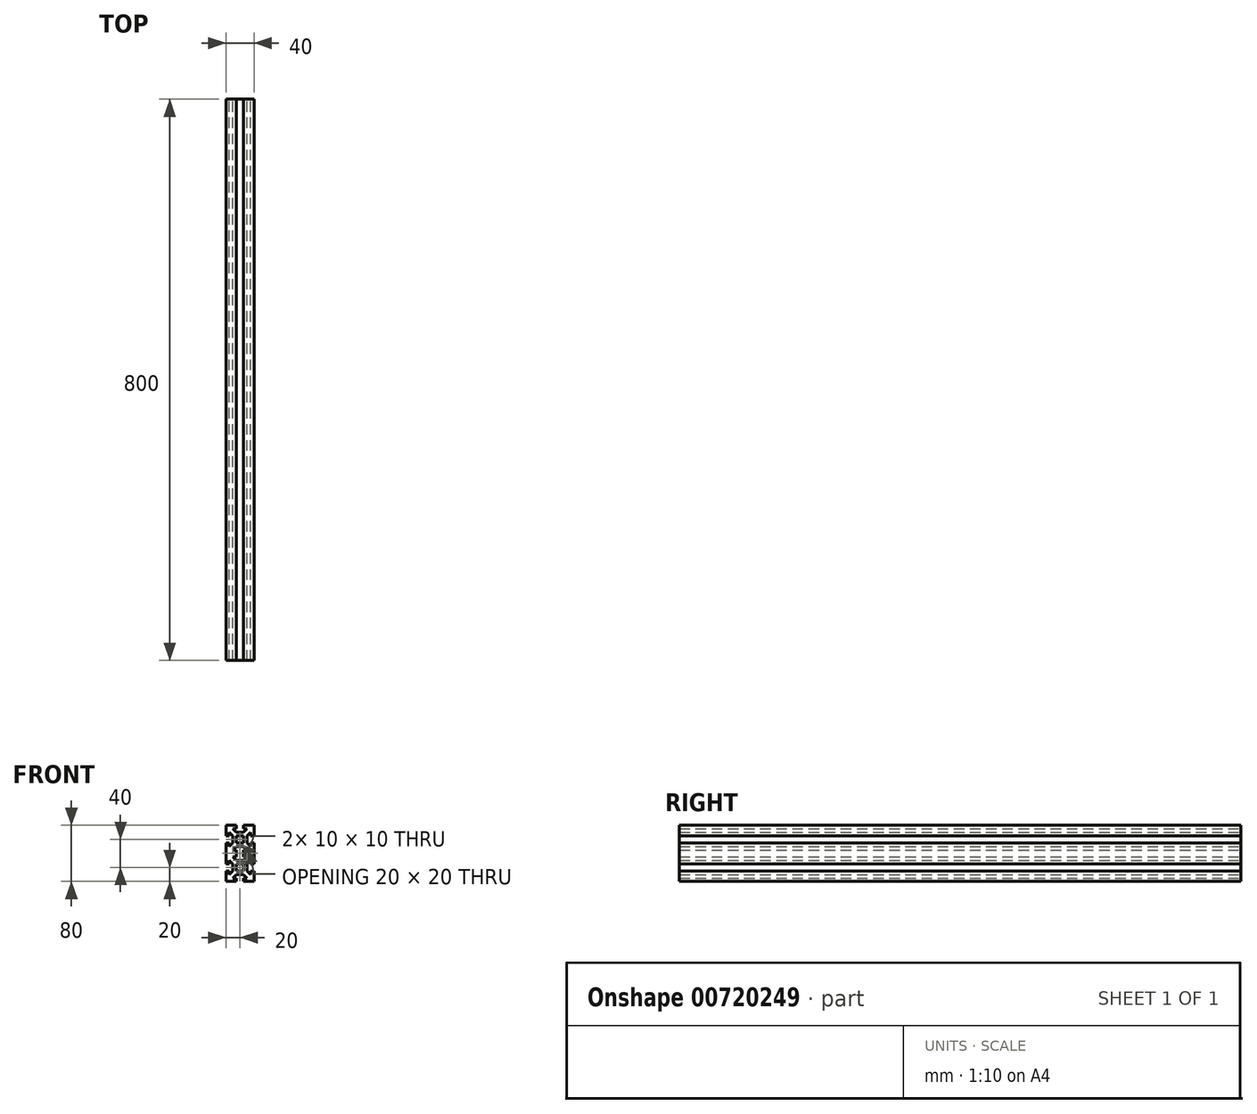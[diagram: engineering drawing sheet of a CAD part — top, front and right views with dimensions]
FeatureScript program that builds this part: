
annotation { "Feature Type Name" : "Feature", "Feature Type Description" : "" }
export const myFeature = defineFeature(function(context is Context, id is Id, definition is map)
    precondition{}
    {
        {
            var Q0;
            Q0=qCreatedBy(makeId("Front.planeOp"),FACE);
            var sketch = newSketch(context, id + "F0", { "sketchPlane" : qUnion([Q0])});
            skLineSegment(sketch, "E0.top", {"start": v(20, -20) * mm, "end": v(5, -20) * mm});
            skLineSegment(sketch, "E0.left", {"start": v(20, 20) * mm, "end": v(20, 5) * mm});
            skLineSegment(sketch, "E0.right", {"start": v(-20, 20) * mm, "end": v(-20, 5) * mm});
            skPoint(sketch, "E0.middle", {"position": v(0, 0) * mm});
            skLineSegment(sketch, "E1", {"start": v(0, 20) * mm, "end": v(0, -20) * mm, "construction": true});
            skLineSegment(sketch, "E2", {"start": v(-20, 0) * mm, "end": v(20, 0) * mm, "construction": true});
            skLineSegment(sketch, "E3", {"start": v(-20, 5) * mm, "end": v(-15, 5) * mm});
            skLineSegment(sketch, "E4", {"start": v(-20, -5) * mm, "end": v(-15, -5) * mm});
            skLineSegment(sketch, "E5", {"start": v(-5, 20) * mm, "end": v(-5, 15) * mm});
            skLineSegment(sketch, "E6", {"start": v(5, 20) * mm, "end": v(5, 15) * mm});
            skLineSegment(sketch, "E7", {"start": v(-10, 15) * mm, "end": v(-5, 15) * mm});
            skLineSegment(sketch, "E8", {"start": v(-10, -15) * mm, "end": v(-5, -15) * mm});
            skLineSegment(sketch, "E9", {"start": v(15, 10) * mm, "end": v(15, 5) * mm});
            skLineSegment(sketch, "E10", {"start": v(-15, 10) * mm, "end": v(-10, 5) * mm});
            skLineSegment(sketch, "E11", {"start": v(-10, 15) * mm, "end": v(-5, 10) * mm});
            skLineSegment(sketch, "E12", {"start": v(-15, -10) * mm, "end": v(-10, -5) * mm});
            skLineSegment(sketch, "E13", {"start": v(-10, -15) * mm, "end": v(-5, -10) * mm});
            skLineSegment(sketch, "E14.trimOffspring", {"start": v(20, -5) * mm, "end": v(20, -20) * mm});
            skLineSegment(sketch, "E15.trimOffspring", {"start": v(-20, -5) * mm, "end": v(-20, -20) * mm});
            skLineSegment(sketch, "E16.trimOffspring", {"start": v(-5, -20) * mm, "end": v(-20, -20) * mm});
            skLineSegment(sketch, "E17.trimOffspring", {"start": v(5, 15) * mm, "end": v(10, 15) * mm});
            skLineSegment(sketch, "E18.trimOffspring", {"start": v(-15, -5) * mm, "end": v(-15, -10) * mm});
            skLineSegment(sketch, "E19.trimOffspring", {"start": v(15, -5) * mm, "end": v(15, -10) * mm});
            skLineSegment(sketch, "E20.trimOffspring", {"start": v(5, -15) * mm, "end": v(10, -15) * mm});
            skLineSegment(sketch, "E21.trimOffspring", {"start": v(-5, 5) * mm, "end": v(-5, -5) * mm});
            skLineSegment(sketch, "E22.trimOffspring", {"start": v(5, 5) * mm, "end": v(5, -5) * mm});
            skLineSegment(sketch, "E23.trimOffspring", {"start": v(15, 5) * mm, "end": v(20, 5) * mm});
            skLineSegment(sketch, "E24.trimOffspring", {"start": v(15, -5) * mm, "end": v(20, -5) * mm});
            skLineSegment(sketch, "E25.trimOffspring", {"start": v(5, -15) * mm, "end": v(5, -20) * mm});
            skLineSegment(sketch, "E26.trimOffspring", {"start": v(-5, -15) * mm, "end": v(-5, -20) * mm});
            skLineSegment(sketch, "E27.trimOffspring", {"start": v(-5, -5) * mm, "end": v(5, -5) * mm});
            skLineSegment(sketch, "E28.trimOffspring", {"start": v(-5, 5) * mm, "end": v(5, 5) * mm});
            skLineSegment(sketch, "E29", {"start": v(10, 5) * mm, "end": v(10, -5) * mm});
            skLineSegment(sketch, "E30", {"start": v(-5, 10) * mm, "end": v(5, 10) * mm});
            skLineSegment(sketch, "E31", {"start": v(-10, 5) * mm, "end": v(-10, -5) * mm});
            skLineSegment(sketch, "E32", {"start": v(-5, -10) * mm, "end": v(5, -10) * mm});
            skLineSegment(sketch, "E33.trimOffspring", {"start": v(-15, 10) * mm, "end": v(-15, 5) * mm});
            skPoint(sketch, "E34.orphan", {"position": v(20, 15) * mm});
            skPoint(sketch, "E35.orphan", {"position": v(20, -15) * mm});
            skPoint(sketch, "E36.orphan", {"position": v(15, -20) * mm});
            skPoint(sketch, "E37.orphan", {"position": v(-15, -20) * mm});
            skLineSegment(sketch, "E38.trimOffspring", {"start": v(-5, 0) * mm, "end": v(0, -5) * mm});
            skLineSegment(sketch, "E39.trimOffspring", {"start": v(-5, 0) * mm, "end": v(0, 5) * mm});
            skLineSegment(sketch, "E40.trimOffspring", {"start": v(0, 5) * mm, "end": v(5, 0) * mm});
            skLineSegment(sketch, "E41.trimOffspring", {"start": v(5, 10) * mm, "end": v(10, 15) * mm});
            skLineSegment(sketch, "E42.trimOffspring", {"start": v(10, 5) * mm, "end": v(15, 10) * mm});
            skLineSegment(sketch, "E43.trimOffspring", {"start": v(10, -5) * mm, "end": v(15, -10) * mm});
            skLineSegment(sketch, "E44.trimOffspring", {"start": v(5, -10) * mm, "end": v(10, -15) * mm});
            skLineSegment(sketch, "E45.trimOffspring", {"start": v(0, -5) * mm, "end": v(5, 0) * mm});
            skLineSegment(sketch, "E46.bottom", {"start": v(20, 60) * mm, "end": v(5, 60) * mm});
            skLineSegment(sketch, "E46.left", {"start": v(20, 60) * mm, "end": v(20, 45) * mm});
            skLineSegment(sketch, "E46.right", {"start": v(-20, 60) * mm, "end": v(-20, 45) * mm});
            skPoint(sketch, "E46.middle", {"position": v(0, 40) * mm});
            skLineSegment(sketch, "E47", {"start": v(0, 60) * mm, "end": v(0, 20) * mm, "construction": true});
            skLineSegment(sketch, "E48", {"start": v(-20, 40) * mm, "end": v(20, 40) * mm, "construction": true});
            skLineSegment(sketch, "E49", {"start": v(-20, 45) * mm, "end": v(-15, 45) * mm});
            skLineSegment(sketch, "E50", {"start": v(-20, 35) * mm, "end": v(-15, 35) * mm});
            skLineSegment(sketch, "E51", {"start": v(-5, 60) * mm, "end": v(-5, 55) * mm});
            skLineSegment(sketch, "E52", {"start": v(5, 60) * mm, "end": v(5, 55) * mm});
            skLineSegment(sketch, "E53", {"start": v(-10, 55) * mm, "end": v(-5, 55) * mm});
            skLineSegment(sketch, "E54", {"start": v(-10, 25) * mm, "end": v(-5, 25) * mm});
            skLineSegment(sketch, "E55", {"start": v(15, 50) * mm, "end": v(15, 45) * mm});
            skLineSegment(sketch, "E56", {"start": v(-15, 50) * mm, "end": v(-10, 45) * mm});
            skLineSegment(sketch, "E57", {"start": v(-10, 55) * mm, "end": v(-5, 50) * mm});
            skLineSegment(sketch, "E58", {"start": v(-15, 30) * mm, "end": v(-10, 35) * mm});
            skLineSegment(sketch, "E59", {"start": v(-10, 25) * mm, "end": v(-5, 30) * mm});
            skLineSegment(sketch, "E60.trimOffspring", {"start": v(20, 35) * mm, "end": v(20, 20) * mm});
            skLineSegment(sketch, "E61.trimOffspring", {"start": v(-20, 35) * mm, "end": v(-20, 20) * mm});
            skLineSegment(sketch, "E62.trimOffspring", {"start": v(-5, 60) * mm, "end": v(-20, 60) * mm});
            skLineSegment(sketch, "E63.trimOffspring", {"start": v(5, 55) * mm, "end": v(10, 55) * mm});
            skLineSegment(sketch, "E64.trimOffspring", {"start": v(-15, 35) * mm, "end": v(-15, 30) * mm});
            skLineSegment(sketch, "E65.trimOffspring", {"start": v(15, 35) * mm, "end": v(15, 30) * mm});
            skLineSegment(sketch, "E66.trimOffspring", {"start": v(5, 25) * mm, "end": v(10, 25) * mm});
            skLineSegment(sketch, "E67.trimOffspring", {"start": v(-5, 45) * mm, "end": v(-5, 35) * mm});
            skLineSegment(sketch, "E68.trimOffspring", {"start": v(5, 45) * mm, "end": v(5, 35) * mm});
            skLineSegment(sketch, "E69.trimOffspring", {"start": v(15, 45) * mm, "end": v(20, 45) * mm});
            skLineSegment(sketch, "E70.trimOffspring", {"start": v(15, 35) * mm, "end": v(20, 35) * mm});
            skLineSegment(sketch, "E71.trimOffspring", {"start": v(5, 25) * mm, "end": v(5, 20) * mm});
            skLineSegment(sketch, "E72.trimOffspring", {"start": v(-5, 25) * mm, "end": v(-5, 20) * mm});
            skLineSegment(sketch, "E73.trimOffspring", {"start": v(-5, 35) * mm, "end": v(5, 35) * mm});
            skLineSegment(sketch, "E74.trimOffspring", {"start": v(-5, 45) * mm, "end": v(5, 45) * mm});
            skLineSegment(sketch, "E75", {"start": v(10, 45) * mm, "end": v(10, 35) * mm});
            skLineSegment(sketch, "E76", {"start": v(-5, 50) * mm, "end": v(5, 50) * mm});
            skLineSegment(sketch, "E77", {"start": v(-10, 45) * mm, "end": v(-10, 35) * mm});
            skLineSegment(sketch, "E78", {"start": v(-5, 30) * mm, "end": v(5, 30) * mm});
            skLineSegment(sketch, "E79.trimOffspring", {"start": v(-15, 50) * mm, "end": v(-15, 45) * mm});
            skPoint(sketch, "E80.orphan", {"position": v(20, 55) * mm});
            skPoint(sketch, "E81.orphan", {"position": v(20, 25) * mm});
            skPoint(sketch, "E82.orphan", {"position": v(15, 20) * mm});
            skLineSegment(sketch, "E83.trimOffspring", {"start": v(-5, 40) * mm, "end": v(0, 35) * mm});
            skLineSegment(sketch, "E84.trimOffspring", {"start": v(-5, 40) * mm, "end": v(0, 45) * mm});
            skLineSegment(sketch, "E85.trimOffspring", {"start": v(0, 45) * mm, "end": v(5, 40) * mm});
            skLineSegment(sketch, "E86.trimOffspring", {"start": v(5, 50) * mm, "end": v(10, 55) * mm});
            skLineSegment(sketch, "E87.trimOffspring", {"start": v(10, 45) * mm, "end": v(15, 50) * mm});
            skLineSegment(sketch, "E88.trimOffspring", {"start": v(10, 35) * mm, "end": v(15, 30) * mm});
            skLineSegment(sketch, "E89.trimOffspring", {"start": v(5, 30) * mm, "end": v(10, 25) * mm});
            skLineSegment(sketch, "E90.trimOffspring", {"start": v(0, 35) * mm, "end": v(5, 40) * mm});
            skSolve(sketch);
        }
        {
            var Q0;
            Q0=makeQuery(id+"F0.imprint","IMPRINT",FACE,{"disambiguationData":[TD([[makeQuery(id+"F0.imprint","IMPRINT",EDGE,{"derivedFrom":sQuery(id+"F0.wireOp",EDGE,"E0.top")}),-1.0]])]});
            extrude(context, id + "F1", {"entities" : qUnion([Q0]), "depth" : 800 * mm, "offsetDistance" : 25 * mm});
        }
    });
